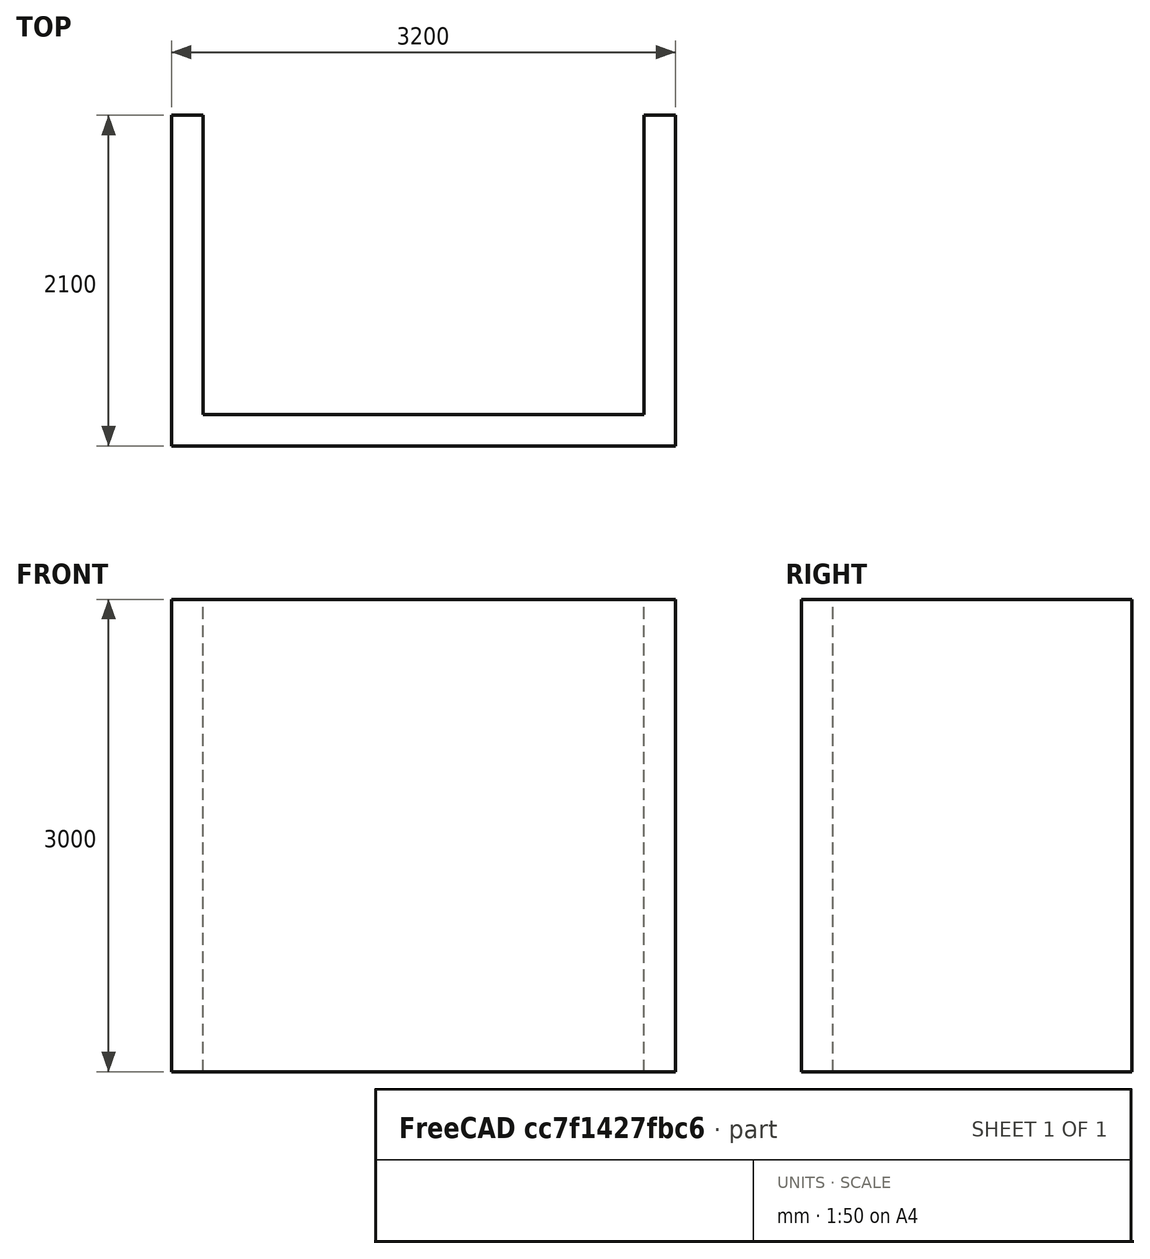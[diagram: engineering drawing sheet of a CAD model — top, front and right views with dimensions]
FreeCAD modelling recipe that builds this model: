
FCSTD DOCUMENT  (FreeCAD 0.19R)
Label: simple_wall
License: Creative Commons Attribution-ShareAlike
LicenseURL: http://creativecommons.org/licenses/by-sa/4.0/
objects: Sketcher::SketchObject×1, Part::FeaturePython×1, App::Part×1
note: 2 computed .brp shape members not serialized (recipe doc carries the construction recipe); baked Part::Feature solids carry a one-line shape summary decoded from their .brp

FEATURE [Sketcher::SketchObject] Sketch  label="wall_profile"
  FullyConstrained = true
  MapMode = 5
  Support = -> [XY_Plane]
  sketch-geometry (4):
    g0: LineSegment StartX=-1500 StartY=1000 StartZ=0 EndX=1500 EndY=1000 EndZ=0
    g1: LineSegment StartX=1500 StartY=1000 StartZ=0 EndX=1500 EndY=-1000 EndZ=0
    g2: LineSegment StartX=1500 StartY=-1000 StartZ=0 EndX=-1500 EndY=-1000 EndZ=0
    g3: LineSegment StartX=-1500 StartY=-1000 StartZ=0 EndX=-1500 EndY=1000 EndZ=0
  constraints (11):
    c: Coincident(g0,g1)
    c: Coincident(g1,g2)
    c: Coincident(g2,g3)
    c: Coincident(g3,g0)
    c: Horizontal(g0)
    c: Horizontal(g2)
    c: Vertical(g1)
    c: Vertical(g3)
    c: Symmetric(g2,g0,g-1)
    c: DistanceX(g2,g2) = 3000
    c: DistanceY(g1,g1) = 2000
FEATURE [Part::FeaturePython] Wall  # Arch/BIM 166 (typed FeaturePython)
  Align = 2
  Area = 21000000
  Base = -> Sketch
  BlockHeight = 0
  BlockLength = 0
  CountBroken = 0
  CountEntire = 0
  Face = 0
  Height = 3000
  HorizontalArea = 1400000
  IfcData = attributes={"GlobalId": {"name": "GlobalId", "type": "IfcGloballyUniqueId", "is_enum": false, "enum_values": []}, "Description": {"... (+533 chars omitted),+1 more (map truncated)
  IfcType = 166
  Joint = 0
  Length = 7000
  MakeBlocks = false
  MoveBase = false
  MoveWithHost = false
  Normal = (0,0,0)
  OffsetFirst = 0
  OffsetSecond = 0
  PerimeterLength = 14400
  PredefinedType = 0
  VerticalArea = 43200000
  Width = 200
FEATURE [App::Part] Part  label="simple_wall_test"
  Group = -> [Sketch,Wall]
  Origin = -> Origin
